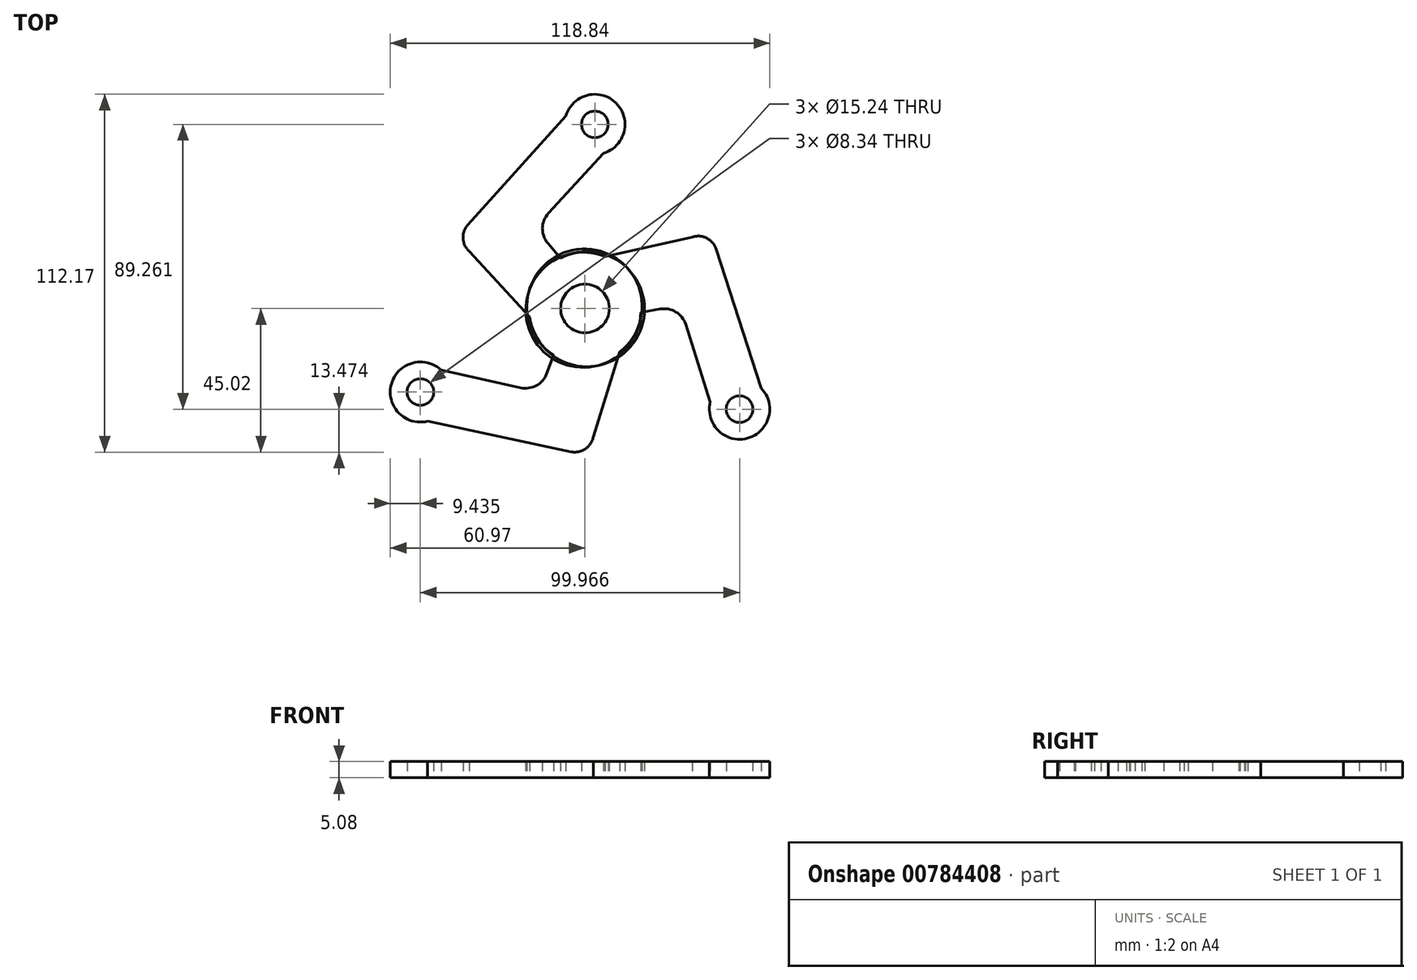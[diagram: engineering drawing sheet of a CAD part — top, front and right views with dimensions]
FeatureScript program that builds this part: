
annotation { "Feature Type Name" : "Feature", "Feature Type Description" : "" }
export const myFeature = defineFeature(function(context is Context, id is Id, definition is map)
    precondition{}
    {
        {
            var Q0;
            Q0=qCreatedBy(makeId("Top.planeOp"),FACE);
            var sketch = newSketch(context, id + "F0", { "sketchPlane" : qUnion([Q0])});
            skCircle(sketch, "E0", {"center": v(3.1, 57.72) * mm, "radius": 9.44 * mm});
            skLineSegment(sketch, "E1.0", {"start": v(-36.67, 26.27) * mm, "end": v(-5.97, 60.31) * mm});
            skLineSegment(sketch, "E2.0", {"start": v(-11.47, 29.81) * mm, "end": v(5.75, 48.66) * mm});
            skLineSegment(sketch, "E3.0", {"start": v(-7.69, 15.81) * mm, "end": v(-11.65, 20.5) * mm});
            skArc(sketch, "E4.filletArc", {"start": v(-11.47, 29.81) * mm, "mid": v(-13.32, 25.19) * mm, "end": v(-11.65, 20.5) * mm});
            skArc(sketch, "E5.filletArc", {"start": v(-36.67, 26.27) * mm, "mid": v(-38.18, 21.97) * mm, "end": v(-36.18, 17.88) * mm});
            skCircle(sketch, "E6.1.5", {"center": v(0.62, -0.2) * mm, "radius": 18.05 * mm});
            skPoint(sketch, "E6.center", {"position": v(0.37, 0.08) * mm});
            skCircle(sketch, "E7", {"center": v(0, 0) * mm, "radius": 7.62 * mm});
            skPoint(sketch, "E8.center", {"position": v(0.1, 0.15) * mm});
            skPoint(sketch, "E9.center", {"position": v(0.17, 0.11) * mm});
            skLineSegment(sketch, "E10", {"start": v(-36.18, 17.88) * mm, "end": v(-17.25, -2.67) * mm});
            skPoint(sketch, "E11.visualSharp", {"position": v(-36.18, 17.88) * mm});
            skLineSegment(sketch, "E11.filletArc", {"start": v(-36.18, 17.88) * mm, "end": v(-36.18, 17.88) * mm});
            skCircle(sketch, "E12", {"center": v(3.1, 57.72) * mm, "radius": 4.17 * mm});
            skSolve(sketch);
        }
        {
            var Q0;
            Q0=makeQuery(id+"F0.imprint","IMPRINT",FACE,{"disambiguationData":[TD([[makeQuery(id+"F0.imprint","IMPRINT",EDGE,{"derivedFrom":sQuery(id+"F0.wireOp",EDGE,"E7")}),-1.0]])]});
            extrude(context, id + "F1", {"entities" : qUnion([Q0]), "depth" : 5.08 * mm, "offsetDistance" : 25.4 * mm});
        }
        {
            var Q0;
            Q0 = qSketchRegion(id + "F0", true);
            extrude(context, id + "F2", {"entities" : qUnion([Q0]), "operationType" : NewBodyOperationType.ADD, "depth" : 5.08 * mm, "offsetDistance" : 25.4 * mm});
        }
        {
            var Q0;
            Q0=makeQuery(id+"F1.opExtrude","SWEPT_BODY",BODY,{"disambiguationData":[OSD([sQuery(id+"F0.wireOp",EDGE,"E6.1.5"),sQuery(id+"F0.wireOp",EDGE,"E7")])]});
            var Q1;
            Q1=makeQuery(id+"F1.opExtrude","CAP_EDGE",EDGE,{"disambiguationData":[OSD([sQuery(id+"F0.wireOp",EDGE,"E7")])],"isStart":false});
            circularPattern(context, id + "F3", {"entities" : qUnion([Q0]), "axis" : qUnion([Q1]), "angle" : 360 * degree, "instanceCount" : 3, "oppositeDirection" : true, "equalSpace" : true});
        }
    });
